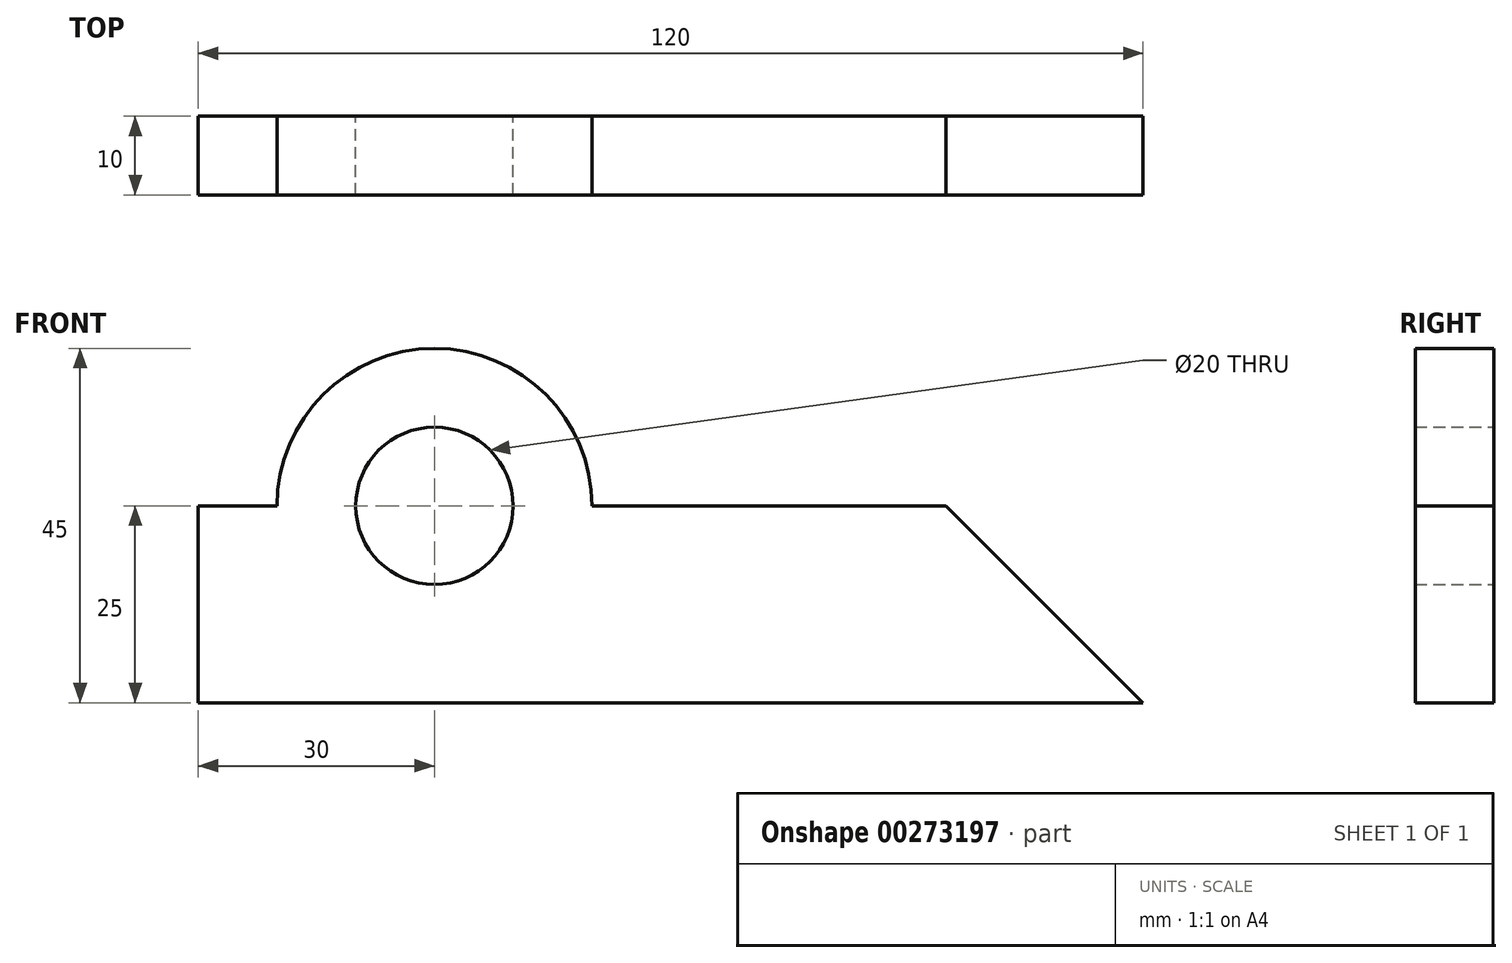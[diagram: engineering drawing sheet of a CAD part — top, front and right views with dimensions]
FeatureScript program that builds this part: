
annotation { "Feature Type Name" : "Feature", "Feature Type Description" : "" }
export const myFeature = defineFeature(function(context is Context, id is Id, definition is map)
    precondition{}
    {
        {
            var Q0;
            Q0=qCreatedBy(makeId("Front.planeOp"),FACE);
            var sketch = newSketch(context, id + "F0", { "sketchPlane" : qUnion([Q0])});
            skLineSegment(sketch, "E0", {"start": v(0, 0) * mm, "end": v(0, 25) * mm});
            skLineSegment(sketch, "E1", {"start": v(95, 25) * mm, "end": v(120, 0) * mm});
            skLineSegment(sketch, "E2", {"start": v(120, 0) * mm, "end": v(0, 0) * mm});
            skCircle(sketch, "E3", {"center": v(30, 25) * mm, "radius": 10 * mm});
            skArc(sketch, "E4", {"start": v(50, 25) * mm, "mid": v(30, 45) * mm, "end": v(10, 25) * mm});
            skLineSegment(sketch, "E5", {"start": v(0, 25) * mm, "end": v(10, 25) * mm});
            skLineSegment(sketch, "E6", {"start": v(50, 25) * mm, "end": v(95, 25) * mm});
            skSolve(sketch);
        }
        {
            var Q0;
            Q0 = qSketchRegion(id + "F0", true);
            extrude(context, id + "F1", {"entities" : qUnion([Q0]), "depth" : 10 * mm});
        }
    });
